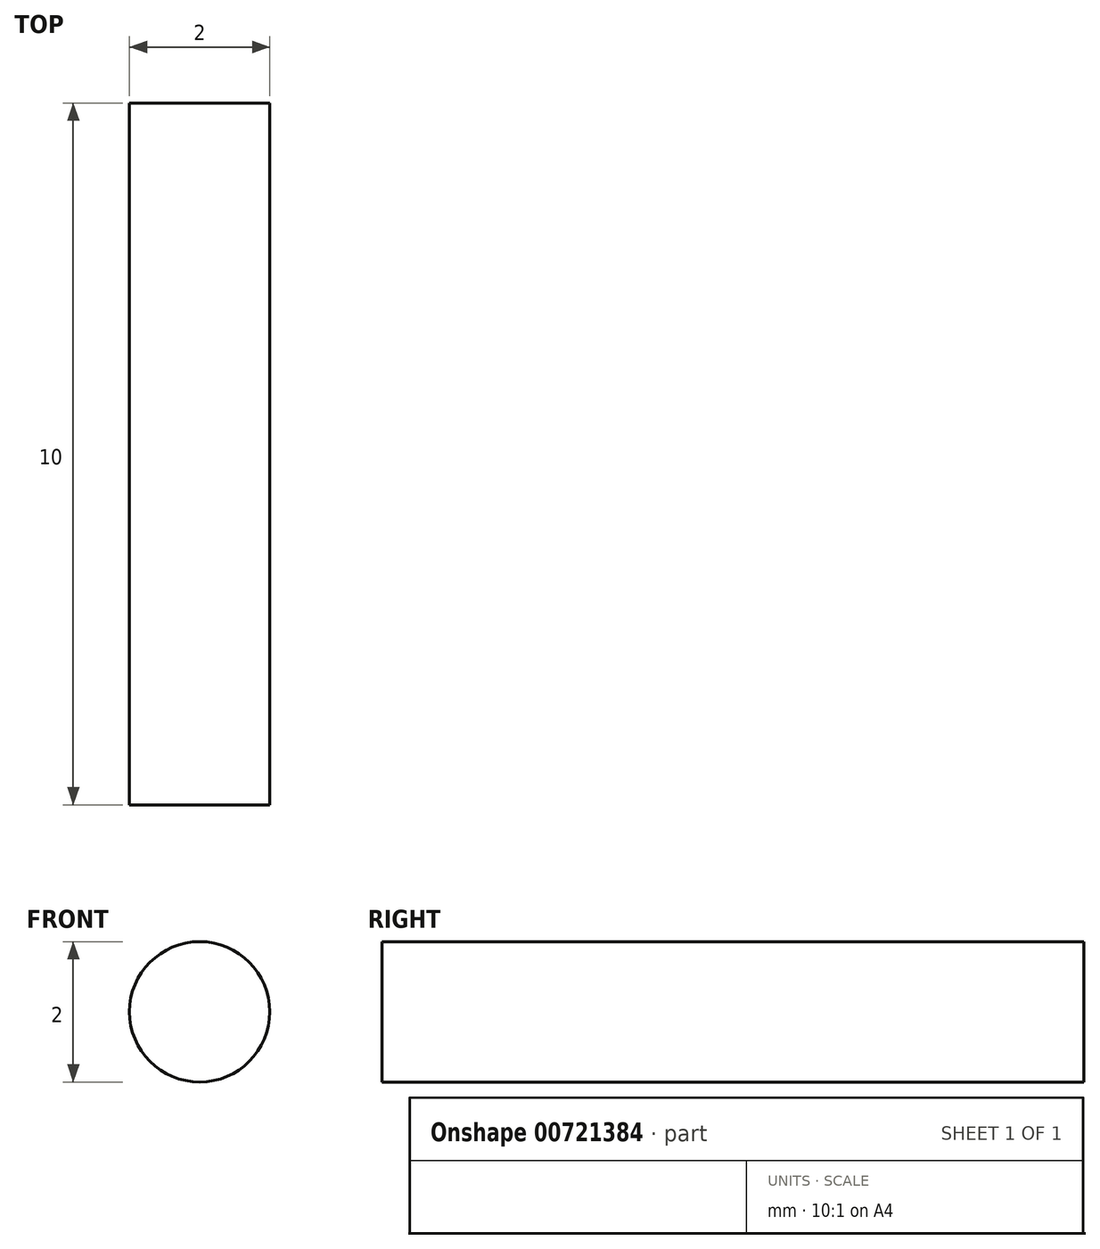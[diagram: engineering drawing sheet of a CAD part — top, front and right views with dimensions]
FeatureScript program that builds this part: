
annotation { "Feature Type Name" : "Feature", "Feature Type Description" : "" }
export const myFeature = defineFeature(function(context is Context, id is Id, definition is map)
    precondition{}
    {
        {
            var Q0;
            Q0=qCreatedBy(makeId("Front.planeOp"),FACE);
            var sketch = newSketch(context, id + "F0", { "sketchPlane" : qUnion([Q0])});
            skCircle(sketch, "E0", {"center": v(0, 0) * mm, "radius": 1 * mm});
            skSolve(sketch);
        }
        {
            var Q0;
            Q0 = qSketchRegion(id + "F0", true);
            extrude(context, id + "F1", {"entities" : qUnion([Q0]), "endBound" : BoundingType.SYMMETRIC, "depth" : 10 * mm, "offsetDistance" : 25.4 * mm});
        }
    });
